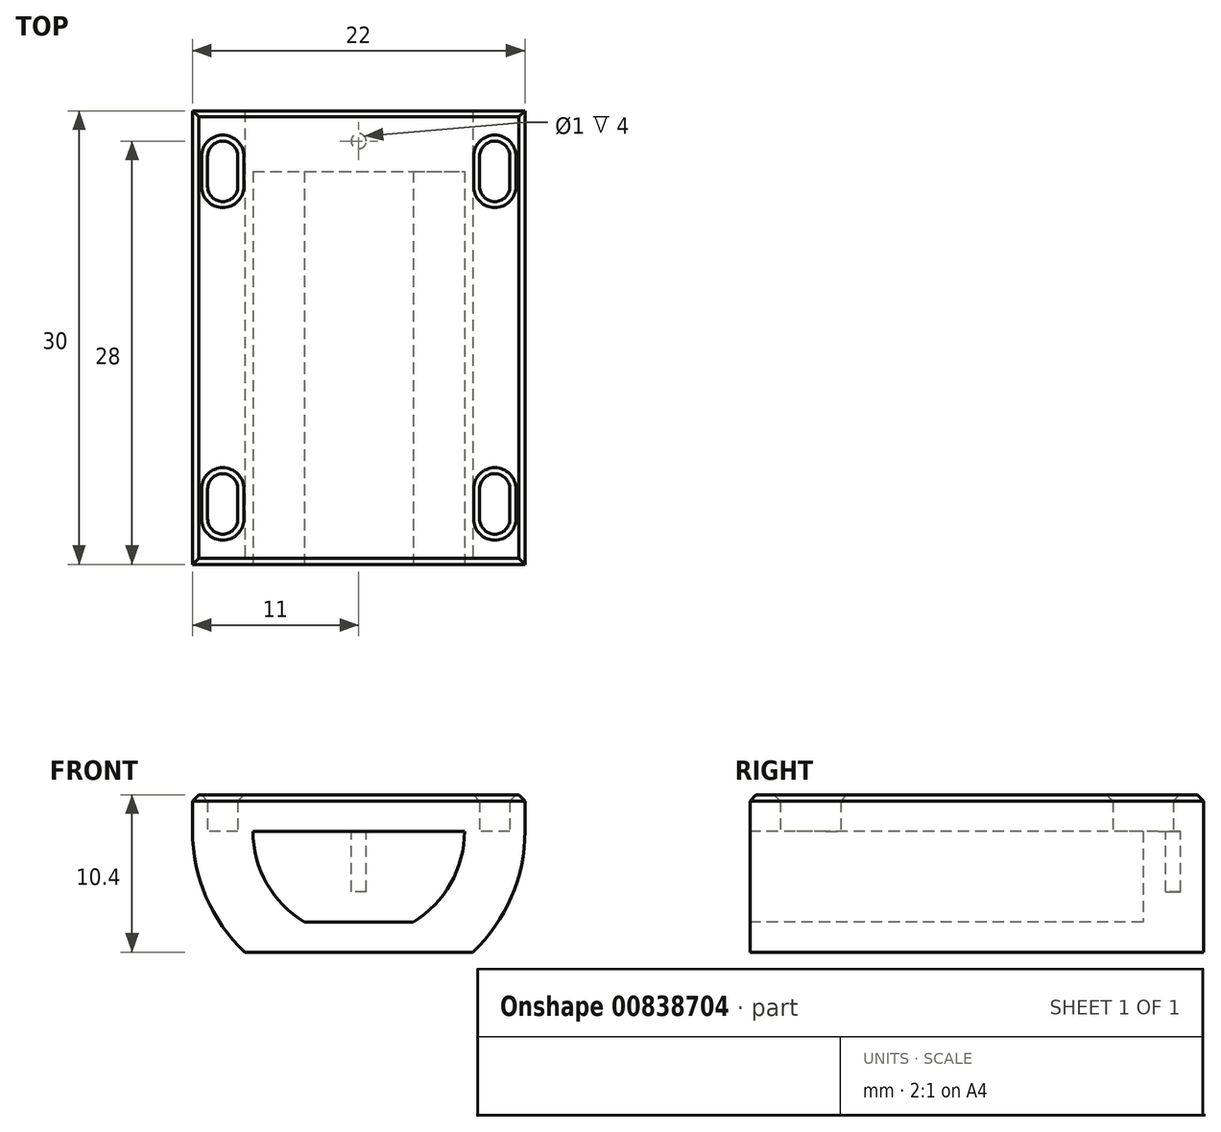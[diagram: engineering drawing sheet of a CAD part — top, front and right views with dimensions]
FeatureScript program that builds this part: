
annotation { "Feature Type Name" : "Feature", "Feature Type Description" : "" }
export const myFeature = defineFeature(function(context is Context, id is Id, definition is map)
    precondition{}
    {
        {
            var Q0;
            Q0=qCreatedBy(makeId("Top.planeOp"),FACE);
            var sketch = newSketch(context, id + "F0", { "sketchPlane" : qUnion([Q0])});
            skLineSegment(sketch, "E0", {"start": v(0, 41.82) * mm, "end": v(0, -8.8) * mm, "construction": true});
            skSolve(sketch);
        }
        {
            var Q0;
            Q0=qCreatedBy(makeId("Top.planeOp"),FACE);
            var sketch = newSketch(context, id + "F1", { "sketchPlane" : qUnion([Q0])});
            skLineSegment(sketch, "E1.bottom", {"start": v(-11, 30) * mm, "end": v(11, 30) * mm});
            skLineSegment(sketch, "E1.top", {"start": v(-11, 0) * mm, "end": v(11, 0) * mm});
            skLineSegment(sketch, "E1.left", {"start": v(-11, 30) * mm, "end": v(-11, 0) * mm});
            skLineSegment(sketch, "E1.right", {"start": v(11, 30) * mm, "end": v(11, 0) * mm});
            skSolve(sketch);
        }
        {
            var Q0;
            Q0=makeQuery(id+"F1.imprint","IMPRINT",FACE,{"disambiguationData":[TD([[makeQuery(id+"F1.imprint","IMPRINT",EDGE,{"derivedFrom":sQuery(id+"F1.wireOp",EDGE,"E1.bottom")}),-1.0]])]});
            extrude(context, id + "F2", {"entities" : qUnion([Q0]), "oppositeDirection" : true, "depth" : 8 * mm, "offsetDistance" : 25 * mm});
        }
        {
            var Q0;
            Q0=makeQuery(id+"F2.opExtrude","SWEPT_FACE",FACE,{"disambiguationData":[OSD([sQuery(id+"F1.wireOp",EDGE,"E1.top")])]});
            var sketch = newSketch(context, id + "F3", { "sketchPlane" : qUnion([Q0])});
            skCircle(sketch, "E2", {"center": v(0, 0) * mm, "radius": 11 * mm});
            skLineSegment(sketch, "E3", {"start": v(-11, 0) * mm, "end": v(-11, -8) * mm});
            skLineSegment(sketch, "E4", {"start": v(-11, -8) * mm, "end": v(-7.55, -8) * mm});
            skLineSegment(sketch, "E5", {"start": v(7.55, -8) * mm, "end": v(11, -8) * mm});
            skLineSegment(sketch, "E6", {"start": v(11, -8) * mm, "end": v(11, 0) * mm});
            skSolve(sketch);
        }
        {
            var Q0;
            {var subQ0=sQuery(id+"F3.wireOp",EDGE,"E3");Q0=makeQuery(id+"F3.imprint","IMPRINT",FACE,{"disambiguationData":[TD([[makeQuery(id+"F3.imprint","IMPRINT",EDGE,{"derivedFrom":subQ0}),-1.0]])]});}
            var Q1;
            {var subQ4=sQuery(id+"F3.wireOp",EDGE,"E5");Q1=makeQuery(id+"F3.imprint","IMPRINT",FACE,{"disambiguationData":[TD([[makeQuery(id+"F3.imprint","IMPRINT",EDGE,{"derivedFrom":subQ4}),1.0]])]});}
            extrude(context, id + "F4", {"entities" : qUnion([Q0, Q1]), "operationType" : NewBodyOperationType.REMOVE, "endBound" : BoundingType.THROUGH_ALL, "oppositeDirection" : true, "depth" : 25 * mm, "offsetDistance" : 25 * mm});
        }
        {
            var Q0;
            {var subQ0=sQuery(id+"F1.wireOp",EDGE,"E1.bottom");var subQ2=sQuery(id+"F1.wireOp",EDGE,"E1.top");var subQ3=sQuery(id+"F1.wireOp",EDGE,"E1.right");var subQ4=sQuery(id+"F1.wireOp",EDGE,"E1.left");Q0=makeQuery(id+"FnuCoxSTm3viMsP_1.boolean.opBoolean","SPLIT",FACE,{"disambiguationData":[TD([makeQuery(id+"F2.opExtrude","SWEPT_FACE",FACE,{"disambiguationData":[OSD([subQ0])]})])],"derivedFrom":makeQuery(id+"F2.opExtrude","CAP_FACE",FACE,{"disambiguationData":[OSD([subQ0,subQ2,subQ4,subQ3])],"isStart":true})});}
            var sketch = newSketch(context, id + "F5", { "sketchPlane" : qUnion([Q0])});
            skLineSegment(sketch, "E7", {"start": v(-9, 5) * mm, "end": v(-9, 3) * mm});
            skLineSegment(sketch, "E8", {"start": v(9, 5) * mm, "end": v(9, 3) * mm});
            skArc(sketch, "E9.0.startCap", {"start": v(-10, 5) * mm, "mid": v(-9, 6) * mm, "end": v(-8, 5) * mm});
            skArc(sketch, "E9.0.endCap", {"start": v(-8, 3) * mm, "mid": v(-9, 2) * mm, "end": v(-10, 3) * mm});
            skLineSegment(sketch, "E9.0.left", {"start": v(-8, 5) * mm, "end": v(-8, 3) * mm});
            skLineSegment(sketch, "E9.0.right", {"start": v(-10, 5) * mm, "end": v(-10, 3) * mm});
            skArc(sketch, "E10.0.startCap", {"start": v(8, 5) * mm, "mid": v(9, 6) * mm, "end": v(10, 5) * mm});
            skArc(sketch, "E10.0.endCap", {"start": v(10, 3) * mm, "mid": v(9, 2) * mm, "end": v(8, 3) * mm});
            skLineSegment(sketch, "E10.0.left", {"start": v(10, 5) * mm, "end": v(10, 3) * mm});
            skLineSegment(sketch, "E10.0.right", {"start": v(8, 5) * mm, "end": v(8, 3) * mm});
            skLineSegment(sketch, "E11", {"start": v(-9, 27) * mm, "end": v(-9, 25) * mm});
            skLineSegment(sketch, "E12", {"start": v(9, 27) * mm, "end": v(9, 25) * mm});
            skArc(sketch, "E13.0.startCap", {"start": v(-10, 27) * mm, "mid": v(-9, 28) * mm, "end": v(-8, 27) * mm});
            skArc(sketch, "E13.0.endCap", {"start": v(-8, 25) * mm, "mid": v(-9, 24) * mm, "end": v(-10, 25) * mm});
            skLineSegment(sketch, "E13.0.left", {"start": v(-8, 27) * mm, "end": v(-8, 25) * mm});
            skLineSegment(sketch, "E13.0.right", {"start": v(-10, 27) * mm, "end": v(-10, 25) * mm});
            skArc(sketch, "E14.0.startCap", {"start": v(8, 27) * mm, "mid": v(9, 28) * mm, "end": v(10, 27) * mm});
            skArc(sketch, "E14.0.endCap", {"start": v(10, 25) * mm, "mid": v(9, 24) * mm, "end": v(8, 25) * mm});
            skLineSegment(sketch, "E14.0.left", {"start": v(10, 27) * mm, "end": v(10, 25) * mm});
            skLineSegment(sketch, "E14.0.right", {"start": v(8, 27) * mm, "end": v(8, 25) * mm});
            skSolve(sketch);
        }
        {
            var Q0;
            Q0=makeQuery(id+"F5.imprint","IMPRINT",FACE,{"disambiguationData":[TD([[makeQuery(id+"F5.imprint","IMPRINT",EDGE,{"derivedFrom":sQuery(id+"F5.wireOp",EDGE,"E9.0.startCap")}),-1.0]])]});
            var Q1;
            Q1=makeQuery(id+"F5.imprint","IMPRINT",FACE,{"disambiguationData":[TD([[makeQuery(id+"F5.imprint","IMPRINT",EDGE,{"derivedFrom":sQuery(id+"F5.wireOp",EDGE,"E10.0.startCap")}),-1.0]])]});
            var Q2;
            Q2=makeQuery(id+"F5.imprint","IMPRINT",FACE,{"disambiguationData":[TD([[makeQuery(id+"F5.imprint","IMPRINT",EDGE,{"derivedFrom":sQuery(id+"F5.wireOp",EDGE,"E13.0.startCap")}),-1.0]])]});
            var Q3;
            Q3=makeQuery(id+"F5.imprint","IMPRINT",FACE,{"disambiguationData":[TD([[makeQuery(id+"F5.imprint","IMPRINT",EDGE,{"derivedFrom":sQuery(id+"F5.wireOp",EDGE,"E14.0.startCap")}),-1.0]])]});
            extrude(context, id + "F6", {"entities" : qUnion([Q0, Q1, Q2, Q3]), "operationType" : NewBodyOperationType.ADD, "depth" : 2.4 * mm, "offsetDistance" : 25 * mm});
        }
        {
            var Q0;
            Q0=makeQuery(id+"F6.opExtrude","CAP_FACE",FACE,{"disambiguationData":[OSD([sQuery(id+"F5.wireOp",EDGE,"E9.0.startCap"),sQuery(id+"F5.wireOp",EDGE,"E9.0.endCap"),sQuery(id+"F5.wireOp",EDGE,"E9.0.left"),sQuery(id+"F5.wireOp",EDGE,"E9.0.right")])],"isStart":false});
            var Q1;
            Q1=makeQuery(id+"F6.opExtrude","CAP_FACE",FACE,{"disambiguationData":[OSD([sQuery(id+"F5.wireOp",EDGE,"E10.0.startCap"),sQuery(id+"F5.wireOp",EDGE,"E10.0.endCap"),sQuery(id+"F5.wireOp",EDGE,"E10.0.left"),sQuery(id+"F5.wireOp",EDGE,"E10.0.right")])],"isStart":false});
            var Q2;
            Q2=makeQuery(id+"F6.opExtrude","CAP_FACE",FACE,{"disambiguationData":[OSD([sQuery(id+"F5.wireOp",EDGE,"E13.0.startCap"),sQuery(id+"F5.wireOp",EDGE,"E13.0.endCap"),sQuery(id+"F5.wireOp",EDGE,"E13.0.left"),sQuery(id+"F5.wireOp",EDGE,"E13.0.right")])],"isStart":false});
            var Q3;
            Q3=makeQuery(id+"F6.opExtrude","CAP_FACE",FACE,{"disambiguationData":[OSD([sQuery(id+"F5.wireOp",EDGE,"E14.0.startCap"),sQuery(id+"F5.wireOp",EDGE,"E14.0.endCap"),sQuery(id+"F5.wireOp",EDGE,"E14.0.left"),sQuery(id+"F5.wireOp",EDGE,"E14.0.right")])],"isStart":false});
            chamfer(context, id + "F7", {"entities" : qUnion([Q0, Q1, Q2, Q3]), "width" : .4 * mm, "tangentPropagation" : true});
        }
        {
            var Q0;
            Q0=makeQuery(id+"F2.opExtrude","SWEPT_FACE",FACE,{"disambiguationData":[OSD([sQuery(id+"F1.wireOp",EDGE,"E1.top")])]});
            var sketch = newSketch(context, id + "F8", { "sketchPlane" : qUnion([Q0])});
            skArc(sketch, "E15", {"start": v(-7, 0) * mm, "mid": v(-6.1, -3.45) * mm, "end": v(-3.6, -6) * mm});
            skLineSegment(sketch, "E16", {"start": v(-3.6, -6) * mm, "end": v(3.6, -6) * mm});
            skLineSegment(sketch, "E17", {"start": v(-7, 0) * mm, "end": v(7, 0) * mm});
            skArc(sketch, "E18.trimOffspring", {"start": v(3.6, -6) * mm, "mid": v(6.1, -3.45) * mm, "end": v(7, 0) * mm});
            skSolve(sketch);
        }
        {
            var Q0;
            {var subQ11=sQuery(id+"F8.wireOp",EDGE,"E15");Q0=makeQuery(id+"F8.imprint","IMPRINT",FACE,{"disambiguationData":[TD([[makeQuery(id+"F8.imprint","IMPRINT",EDGE,{"derivedFrom":subQ11}),1.0]])]});}
            extrude(context, id + "F9", {"entities" : qUnion([Q0]), "operationType" : NewBodyOperationType.REMOVE, "oppositeDirection" : true, "depth" : 26 * mm, "offsetDistance" : 25 * mm});
        }
        {
            var Q0;
            Q0=makeQuery(id+"F2.opExtrude","CAP_FACE",FACE,{"disambiguationData":[OSD([sQuery(id+"F1.wireOp",EDGE,"E1.bottom"),sQuery(id+"F1.wireOp",EDGE,"E1.top"),sQuery(id+"F1.wireOp",EDGE,"E1.left"),sQuery(id+"F1.wireOp",EDGE,"E1.right")])],"isStart":true});
            var sketch = newSketch(context, id + "F10", { "sketchPlane" : qUnion([Q0])});
            skCircle(sketch, "E19", {"center": v(0, 28) * mm, "radius": 0.5 * mm});
            skSolve(sketch);
        }
        {
            var Q0;
            Q0=makeQuery(id+"F10.imprint","IMPRINT",FACE,{"disambiguationData":[TD([[makeQuery(id+"F10.imprint","IMPRINT",EDGE,{"derivedFrom":sQuery(id+"F10.wireOp",EDGE,"E19")}),1.0]])]});
            extrude(context, id + "F11", {"entities" : qUnion([Q0]), "operationType" : NewBodyOperationType.REMOVE, "oppositeDirection" : true, "depth" : 4 * mm, "offsetDistance" : 25 * mm});
        }
    });
